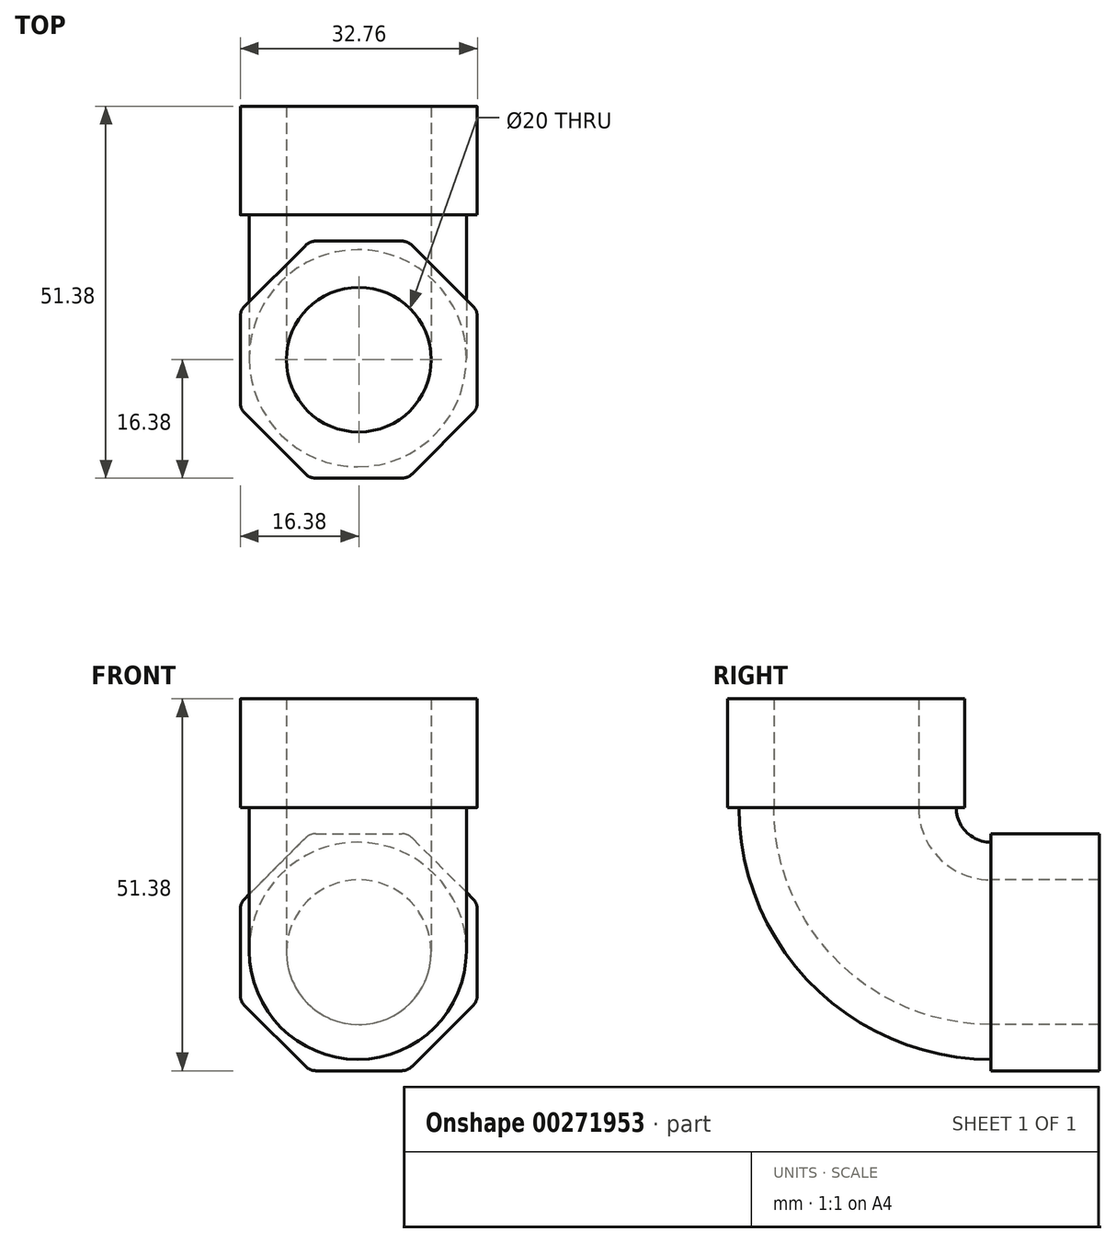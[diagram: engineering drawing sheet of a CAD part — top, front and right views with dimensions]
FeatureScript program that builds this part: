
annotation { "Feature Type Name" : "Feature", "Feature Type Description" : "" }
export const myFeature = defineFeature(function(context is Context, id is Id, definition is map)
    precondition{}
    {
        {
            var Q0;
            Q0=qCreatedBy(makeId("Front.planeOp"),FACE);
            var sketch = newSketch(context, id + "F0", { "sketchPlane" : qUnion([Q0])});
            skCircle(sketch, "E0", {"center": v(-0.13, 0.2) * mm, "radius": 15 * mm});
            skCircle(sketch, "E1", {"center": v(0, 0) * mm, "radius": 10 * mm});
            skSolve(sketch);
        }
        {
            var Q0;
            Q0=qCreatedBy(makeId("Right.planeOp"),FACE);
            var sketch = newSketch(context, id + "F1", { "sketchPlane" : qUnion([Q0])});
            skArc(sketch, "E2", {"start": v(-20, 20) * mm, "mid": v(-14.14, 5.86) * mm, "end": v(0, 0) * mm});
            skLineSegment(sketch, "E3", {"start": v(0, 20) * mm, "end": v(-20, 20) * mm, "construction": true});
            skSolve(sketch);
        }
        {
            var Q0;
            Q0=makeQuery(id+"F0.imprint","IMPRINT",FACE,{"disambiguationData":[TD([[makeQuery(id+"F0.imprint","IMPRINT",EDGE,{"derivedFrom":sQuery(id+"F0.wireOp",EDGE,"E0")}),1.0]])]});
            var Q1;
            Q1=sQuery(id+"F1.wireOp",EDGE,"E2");
            sweep(context, id + "F2", {"profiles" : qUnion([Q0]), "path" : qUnion([Q1])});
        }
        {
            var Q0;
            Q0=qCreatedBy(makeId("Front.planeOp"),FACE);
            var sketch = newSketch(context, id + "F3", { "sketchPlane" : qUnion([Q0])});
            skCircle(sketch, "E4", {"center": v(0, 0) * mm, "radius": 10 * mm});
            skCircle(sketch, "E5.cCircle", {"center": v(0, 0) * mm, "radius": 16.38 * mm, "construction": true});
            skLineSegment(sketch, "E5.0", {"start": v(-5.95, 16.38) * mm, "end": v(5.95, 16.38) * mm});
            skLineSegment(sketch, "E5.1", {"start": v(7.37, 15.79) * mm, "end": v(15.79, 7.37) * mm});
            skLineSegment(sketch, "E5.2", {"start": v(16.38, 5.95) * mm, "end": v(16.38, -5.95) * mm});
            skLineSegment(sketch, "E5.3", {"start": v(15.79, -7.37) * mm, "end": v(7.37, -15.79) * mm});
            skLineSegment(sketch, "E5.4", {"start": v(5.95, -16.38) * mm, "end": v(-5.95, -16.38) * mm});
            skLineSegment(sketch, "E5.5", {"start": v(-7.37, -15.79) * mm, "end": v(-15.79, -7.37) * mm});
            skLineSegment(sketch, "E5.6", {"start": v(-16.38, -5.95) * mm, "end": v(-16.38, 5.95) * mm});
            skLineSegment(sketch, "E5.7", {"start": v(-15.79, 7.37) * mm, "end": v(-7.37, 15.79) * mm});
            skPoint(sketch, "E5.0.midPoint", {"position": v(0, 16.38) * mm});
            skPoint(sketch, "E6.visualSharp", {"position": v(6.78, 16.38) * mm});
            skArc(sketch, "E6.filletArc", {"start": v(7.37, 15.79) * mm, "mid": v(6.72, 16.22) * mm, "end": v(5.95, 16.38) * mm});
            skPoint(sketch, "E7.visualSharp", {"position": v(-6.78, 16.38) * mm});
            skArc(sketch, "E7.filletArc", {"start": v(-5.95, 16.38) * mm, "mid": v(-6.72, 16.22) * mm, "end": v(-7.37, 15.79) * mm});
            skPoint(sketch, "E8.visualSharp", {"position": v(-16.38, 6.78) * mm});
            skArc(sketch, "E8.filletArc", {"start": v(-15.79, 7.37) * mm, "mid": v(-16.22, 6.72) * mm, "end": v(-16.38, 5.95) * mm});
            skPoint(sketch, "E9.visualSharp", {"position": v(16.38, 6.78) * mm});
            skArc(sketch, "E9.filletArc", {"start": v(16.38, 5.95) * mm, "mid": v(16.22, 6.72) * mm, "end": v(15.79, 7.37) * mm});
            skPoint(sketch, "E10.visualSharp", {"position": v(16.38, -6.78) * mm});
            skArc(sketch, "E10.filletArc", {"start": v(15.79, -7.37) * mm, "mid": v(16.22, -6.72) * mm, "end": v(16.38, -5.95) * mm});
            skPoint(sketch, "E11.visualSharp", {"position": v(6.78, -16.38) * mm});
            skArc(sketch, "E11.filletArc", {"start": v(5.95, -16.38) * mm, "mid": v(6.72, -16.22) * mm, "end": v(7.37, -15.79) * mm});
            skPoint(sketch, "E12.visualSharp", {"position": v(-6.78, -16.38) * mm});
            skArc(sketch, "E12.filletArc", {"start": v(-7.37, -15.79) * mm, "mid": v(-6.72, -16.22) * mm, "end": v(-5.95, -16.38) * mm});
            skPoint(sketch, "E13.visualSharp", {"position": v(-16.38, -6.78) * mm});
            skArc(sketch, "E13.filletArc", {"start": v(-16.38, -5.95) * mm, "mid": v(-16.22, -6.72) * mm, "end": v(-15.79, -7.37) * mm});
            skSolve(sketch);
        }
        {
            var Q0;
            Q0 = qSketchRegion(id + "F3", true);
            extrude(context, id + "F4", {"entities" : qUnion([Q0]), "operationType" : NewBodyOperationType.ADD, "oppositeDirection" : true, "depth" : 15 * mm});
        }
        {
            var Q0;
            Q0=makeQuery(id+"F2.opSweep","CAP_FACE",FACE,{"disambiguationData":[OSD([sQuery(id+"F0.wireOp",EDGE,"E0"),sQuery(id+"F0.wireOp",EDGE,"E1"),sQuery(id+"F1.wireOp",VERTEX,"E2.start")])],"isStart":false});
            var sketch = newSketch(context, id + "F5", { "sketchPlane" : qUnion([Q0])});
            skCircle(sketch, "E14", {"center": v(0, -20) * mm, "radius": 10 * mm});
            skCircle(sketch, "E15.cCircle", {"center": v(0, -20) * mm, "radius": 16.38 * mm, "construction": true});
            skLineSegment(sketch, "E15.0", {"start": v(-5.95, -3.62) * mm, "end": v(5.95, -3.62) * mm});
            skLineSegment(sketch, "E15.1", {"start": v(7.37, -4.21) * mm, "end": v(15.79, -12.63) * mm});
            skLineSegment(sketch, "E15.2", {"start": v(16.38, -14.05) * mm, "end": v(16.38, -25.95) * mm});
            skLineSegment(sketch, "E15.3", {"start": v(15.79, -27.37) * mm, "end": v(7.37, -35.79) * mm});
            skLineSegment(sketch, "E15.4", {"start": v(5.95, -36.38) * mm, "end": v(-5.95, -36.38) * mm});
            skLineSegment(sketch, "E15.5", {"start": v(-7.37, -35.79) * mm, "end": v(-15.79, -27.37) * mm});
            skLineSegment(sketch, "E15.6", {"start": v(-16.38, -25.95) * mm, "end": v(-16.38, -14.05) * mm});
            skLineSegment(sketch, "E15.7", {"start": v(-15.79, -12.63) * mm, "end": v(-7.37, -4.21) * mm});
            skPoint(sketch, "E15.0.midPoint", {"position": v(0, -3.62) * mm});
            skPoint(sketch, "E16.visualSharp", {"position": v(6.78, -3.62) * mm});
            skArc(sketch, "E16.filletArc", {"start": v(7.37, -4.21) * mm, "mid": v(6.72, -3.78) * mm, "end": v(5.95, -3.62) * mm});
            skPoint(sketch, "E17.visualSharp", {"position": v(-6.78, -3.62) * mm});
            skArc(sketch, "E17.filletArc", {"start": v(-5.95, -3.62) * mm, "mid": v(-6.72, -3.78) * mm, "end": v(-7.37, -4.21) * mm});
            skPoint(sketch, "E18.visualSharp", {"position": v(-16.38, -13.22) * mm});
            skArc(sketch, "E18.filletArc", {"start": v(-15.79, -12.63) * mm, "mid": v(-16.22, -13.28) * mm, "end": v(-16.38, -14.05) * mm});
            skPoint(sketch, "E19.visualSharp", {"position": v(16.38, -13.22) * mm});
            skArc(sketch, "E19.filletArc", {"start": v(16.38, -14.05) * mm, "mid": v(16.22, -13.28) * mm, "end": v(15.79, -12.63) * mm});
            skPoint(sketch, "E20.visualSharp", {"position": v(16.38, -26.78) * mm});
            skArc(sketch, "E20.filletArc", {"start": v(15.79, -27.37) * mm, "mid": v(16.22, -26.72) * mm, "end": v(16.38, -25.95) * mm});
            skPoint(sketch, "E21.visualSharp", {"position": v(6.78, -36.38) * mm});
            skArc(sketch, "E21.filletArc", {"start": v(5.95, -36.38) * mm, "mid": v(6.72, -36.22) * mm, "end": v(7.37, -35.79) * mm});
            skPoint(sketch, "E22.visualSharp", {"position": v(-6.78, -36.38) * mm});
            skArc(sketch, "E22.filletArc", {"start": v(-7.37, -35.79) * mm, "mid": v(-6.72, -36.22) * mm, "end": v(-5.95, -36.38) * mm});
            skPoint(sketch, "E23.visualSharp", {"position": v(-16.38, -26.78) * mm});
            skArc(sketch, "E23.filletArc", {"start": v(-16.38, -25.95) * mm, "mid": v(-16.22, -26.72) * mm, "end": v(-15.79, -27.37) * mm});
            skSolve(sketch);
        }
        {
            var Q0;
            Q0=makeQuery(id+"F5.imprint","IMPRINT",FACE,{"disambiguationData":[TD([[makeQuery(id+"F5.imprint","IMPRINT",EDGE,{"derivedFrom":sQuery(id+"F5.wireOp",EDGE,"E14")}),-1.0]])]});
            var Q1;
            Q1=makeQuery(id+"F5.imprint","IMPRINT",FACE,{"disambiguationData":[TD([[makeQuery(id+"F5.imprint","IMPRINT",EDGE,{"derivedFrom":sQuery(id+"F5.wireOp",EDGE,"E15.0")}),-1.0]])]});
            extrude(context, id + "F6", {"entities" : qUnion([Q0, Q1]), "operationType" : NewBodyOperationType.ADD, "depth" : 15 * mm});
        }
    });
